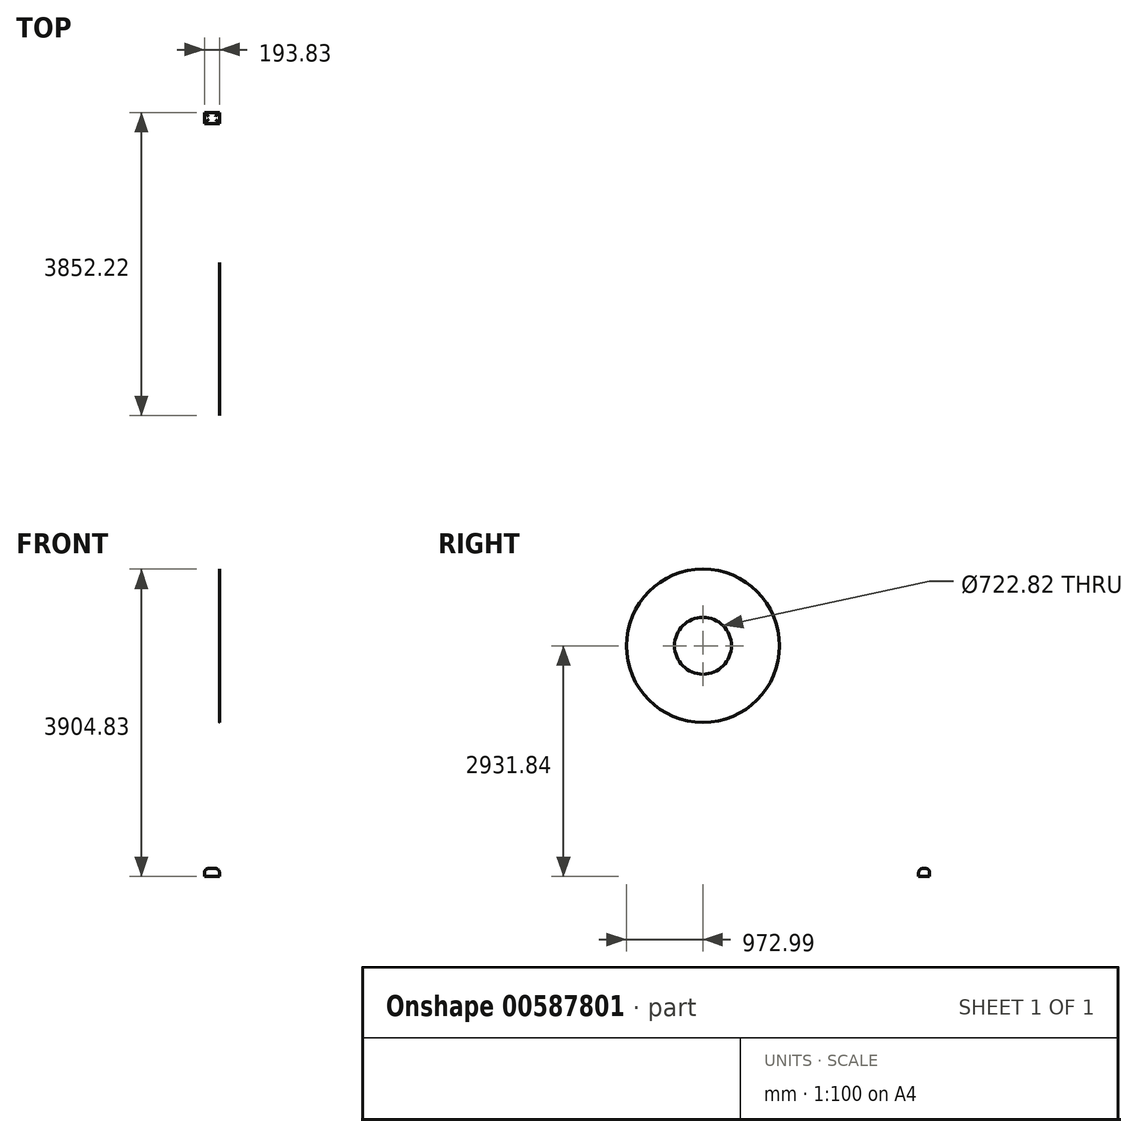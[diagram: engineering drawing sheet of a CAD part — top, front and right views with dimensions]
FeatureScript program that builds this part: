
annotation { "Feature Type Name" : "Feature", "Feature Type Description" : "" }
export const myFeature = defineFeature(function(context is Context, id is Id, definition is map)
    precondition{}
    {
        {
            var Q0;
            Q0=qCreatedBy(makeId("Top.planeOp"),FACE);
            var sketch = newSketch(context, id + "F0", { "sketchPlane" : qUnion([Q0])});
            skLineSegment(sketch, "E0.bottom", {"start": v(0, 0) * mm, "end": v(-190.83, 0) * mm});
            skLineSegment(sketch, "E0.top", {"start": v(0, -139.83) * mm, "end": v(-190.83, -139.83) * mm});
            skLineSegment(sketch, "E0.left", {"start": v(0, 0) * mm, "end": v(0, -139.83) * mm});
            skLineSegment(sketch, "E0.right", {"start": v(-190.83, 0) * mm, "end": v(-190.83, -139.83) * mm});
            skSolve(sketch);
        }
        {
            var Q0;
            Q0=makeQuery(id+"F0.imprint","IMPRINT",FACE,{"disambiguationData":[TD([[makeQuery(id+"F0.imprint","IMPRINT",EDGE,{"derivedFrom":sQuery(id+"F0.wireOp",EDGE,"E0.bottom")}),1.0]])]});
            extrude(context, id + "F1", {"entities" : qUnion([Q0]), "oppositeDirection" : true, "depth" : 102 * mm, "offsetDistance" : 25 * mm});
        }
        {
            var Q0;
            Q0=makeQuery(id+"F1.opExtrude","CAP_FACE",FACE,{"disambiguationData":[OSD([sQuery(id+"F0.wireOp",EDGE,"E0.bottom"),sQuery(id+"F0.wireOp",EDGE,"E0.top"),sQuery(id+"F0.wireOp",EDGE,"E0.left"),sQuery(id+"F0.wireOp",EDGE,"E0.right")])],"isStart":true});
            fillet(context, id + "F2", {"entities" : qUnion([Q0]), "radius" : 50 * mm, "tangentPropagation" : true, "allowEdgeOverflow" : false});
        }
        {
            var Q0;
            Q0=qCreatedBy(makeId("Right.planeOp"),FACE);
            var sketch = newSketch(context, id + "F3", { "sketchPlane" : qUnion([Q0])});
            skCircle(sketch, "E1", {"center": v(2973.35, -1612.1) * mm, "radius": 1091.22 * mm});
            skCircle(sketch, "E2", {"center": v(591.29, -365.18) * mm, "radius": 10.9 * mm});
            skSolve(sketch);
        }
        {
            var Q0;
            Q0=makeQuery(id+"F3.imprint","IMPRINT",FACE,{"disambiguationData":[TD([[makeQuery(id+"F3.imprint","IMPRINT",EDGE,{"derivedFrom":sQuery(id+"F3.wireOp",EDGE,"E1")}),1.0]])]});
            var sketch = newSketch(context, id + "F4", { "sketchPlane" : qUnion([Q0])});
            skCircle(sketch, "E3", {"center": v(2948, -1572.5) * mm, "radius": 423.48 * mm});
            skCircle(sketch, "E4", {"center": v(-2879.23, 2829.84) * mm, "radius": 972.99 * mm});
            skCircle(sketch, "E5", {"center": v(-2879.23, 2829.84) * mm, "radius": 361.4 * mm});
            skSolve(sketch);
        }
        {
            var Q0;
            Q0=makeQuery(id+"F4.imprint","IMPRINT",FACE,{"disambiguationData":[TD([[makeQuery(id+"F4.imprint","IMPRINT",EDGE,{"derivedFrom":sQuery(id+"F4.wireOp",EDGE,"E4")}),1.0]])]});
            extrude(context, id + "F5", {"entities" : qUnion([Q0]), "depth" : 3 * mm, "offsetDistance" : 25 * mm});
        }
    });
